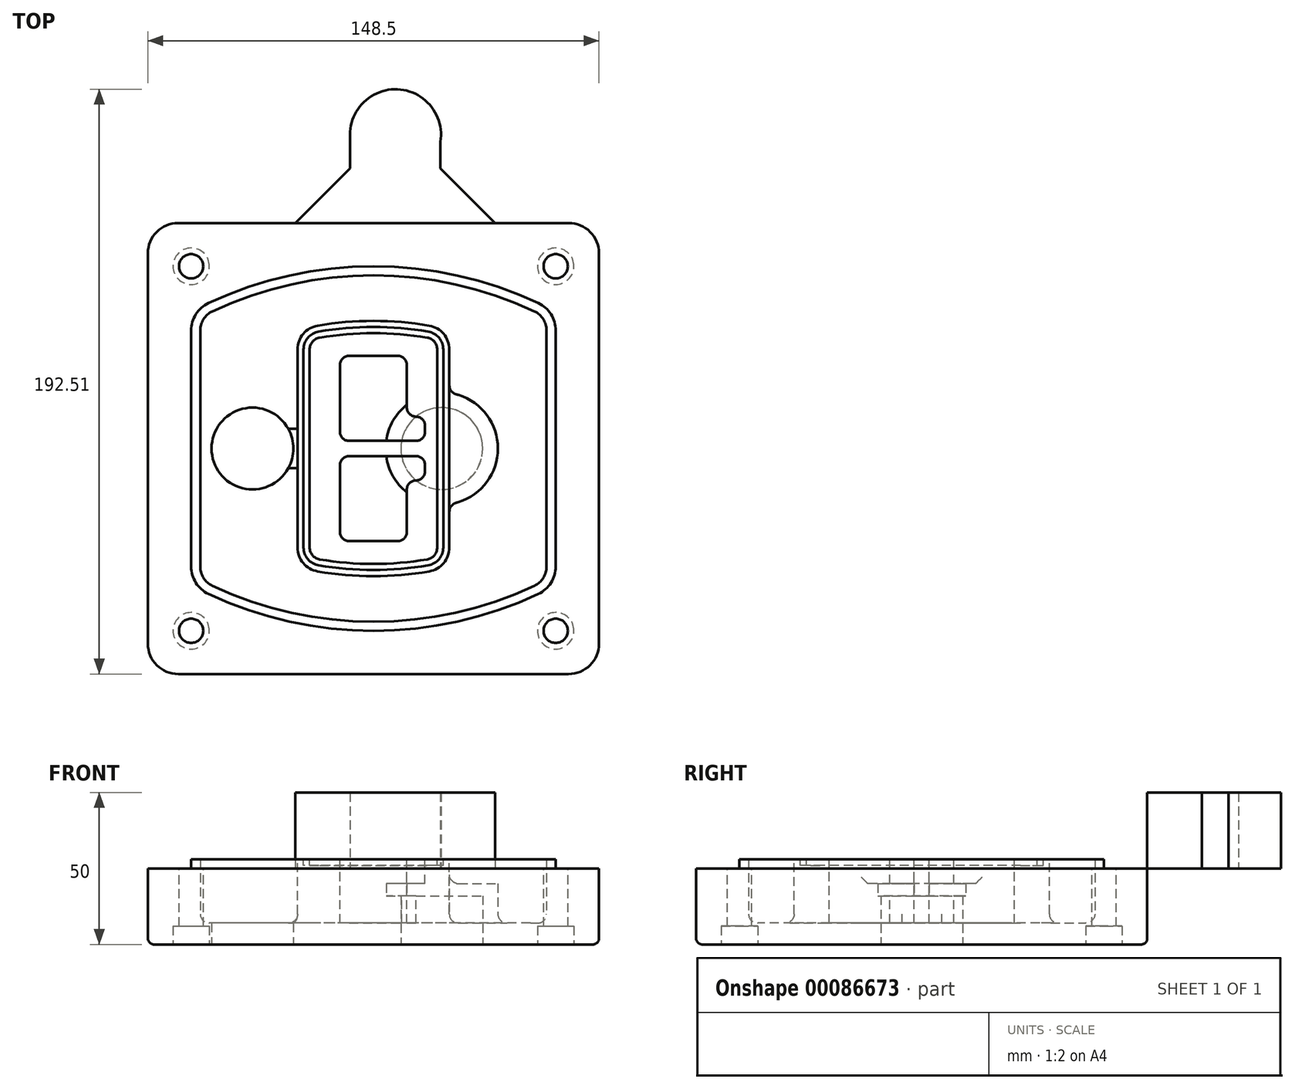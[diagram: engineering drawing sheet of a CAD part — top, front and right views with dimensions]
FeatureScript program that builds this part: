
annotation { "Feature Type Name" : "Feature", "Feature Type Description" : "" }
export const myFeature = defineFeature(function(context is Context, id is Id, definition is map)
    precondition{}
    {
        {
            var Q0;
            Q0=qCreatedBy(makeId("Top.planeOp"),FACE);
            var sketch = newSketch(context, id + "F0", { "sketchPlane" : qUnion([Q0])});
            skPoint(sketch, "E0.rect.middle", {"position": v(0, 0) * mm});
            skLineSegment(sketch, "E1.bottom", {"start": v(-64.25, -74.25) * mm, "end": v(64.25, -74.25) * mm});
            skLineSegment(sketch, "E1.top", {"start": v(-64.25, 74.25) * mm, "end": v(64.25, 74.25) * mm});
            skLineSegment(sketch, "E1.left", {"start": v(-74.25, -64.25) * mm, "end": v(-74.25, 64.25) * mm});
            skLineSegment(sketch, "E1.right", {"start": v(74.25, -64.25) * mm, "end": v(74.25, 64.25) * mm});
            skLineSegment(sketch, "E2", {"start": v(-74.25, 74.25) * mm, "end": v(74.25, -74.25) * mm, "construction": true});
            skLineSegment(sketch, "E3", {"start": v(74.25, 74.25) * mm, "end": v(-74.25, -74.25) * mm, "construction": true});
            skCircle(sketch, "E4", {"center": v(-60, 60) * mm, "radius": 4 * mm});
            skCircle(sketch, "E5", {"center": v(60, 60) * mm, "radius": 4 * mm});
            skCircle(sketch, "E6", {"center": v(60, -60) * mm, "radius": 4 * mm});
            skCircle(sketch, "E7", {"center": v(-60, -60) * mm, "radius": 4 * mm});
            skLineSegment(sketch, "E8", {"start": v(-60, 60) * mm, "end": v(60, 60) * mm, "construction": true});
            skLineSegment(sketch, "E9", {"start": v(60, 60) * mm, "end": v(60, -60) * mm, "construction": true});
            skLineSegment(sketch, "E10", {"start": v(60, -60) * mm, "end": v(-60, -60) * mm, "construction": true});
            skLineSegment(sketch, "E11", {"start": v(-60, -60) * mm, "end": v(-60, 60) * mm, "construction": true});
            skLineSegment(sketch, "E12", {"start": v(-60, 38.83) * mm, "end": v(-60, -38.83) * mm});
            skLineSegment(sketch, "E13", {"start": v(60, 38.83) * mm, "end": v(60, -38.83) * mm});
            skArc(sketch, "E14", {"start": v(54.26, 47.88) * mm, "mid": v(0, 60) * mm, "end": v(-54.26, 47.88) * mm});
            skArc(sketch, "E15", {"start": v(-54.26, -47.88) * mm, "mid": v(0, -60) * mm, "end": v(54.26, -47.88) * mm});
            skLineSegment(sketch, "E16", {"start": v(-60, 0) * mm, "end": v(60, 0) * mm, "construction": true});
            skPoint(sketch, "E17.visualSharp", {"position": v(-60, -45) * mm});
            skArc(sketch, "E17.filletArc", {"start": v(-60, -38.83) * mm, "mid": v(-58.44, -44.2) * mm, "end": v(-54.26, -47.88) * mm});
            skPoint(sketch, "E18.visualSharp", {"position": v(-60, 45) * mm});
            skArc(sketch, "E18.filletArc", {"start": v(-54.26, 47.88) * mm, "mid": v(-58.44, 44.2) * mm, "end": v(-60, 38.83) * mm});
            skPoint(sketch, "E19.visualSharp", {"position": v(60, 45) * mm});
            skArc(sketch, "E19.filletArc", {"start": v(60, 38.83) * mm, "mid": v(58.44, 44.2) * mm, "end": v(54.26, 47.88) * mm});
            skPoint(sketch, "E20.visualSharp", {"position": v(60, -45) * mm});
            skArc(sketch, "E20.filletArc", {"start": v(54.26, -47.88) * mm, "mid": v(58.44, -44.2) * mm, "end": v(60, -38.83) * mm});
            skPoint(sketch, "E21.visualSharp", {"position": v(-74.25, 74.25) * mm});
            skArc(sketch, "E21.filletArc", {"start": v(-64.25, 74.25) * mm, "mid": v(-71.32, 71.32) * mm, "end": v(-74.25, 64.25) * mm});
            skPoint(sketch, "E22.visualSharp", {"position": v(74.25, 74.25) * mm});
            skArc(sketch, "E22.filletArc", {"start": v(74.25, 64.25) * mm, "mid": v(71.32, 71.32) * mm, "end": v(64.25, 74.25) * mm});
            skPoint(sketch, "E23.visualSharp", {"position": v(74.25, -74.25) * mm});
            skArc(sketch, "E23.filletArc", {"start": v(64.25, -74.25) * mm, "mid": v(71.32, -71.32) * mm, "end": v(74.25, -64.25) * mm});
            skPoint(sketch, "E24.visualSharp", {"position": v(-74.25, -74.25) * mm});
            skArc(sketch, "E24.filletArc", {"start": v(-74.25, -64.25) * mm, "mid": v(-71.32, -71.32) * mm, "end": v(-64.25, -74.25) * mm});
            skArc(sketch, "E25.0", {"start": v(57, 38.83) * mm, "mid": v(55.9, 42.58) * mm, "end": v(52.98, 45.17) * mm});
            skLineSegment(sketch, "E25.1", {"start": v(57, 38.83) * mm, "end": v(57, -38.83) * mm});
            skArc(sketch, "E25.2", {"start": v(52.98, -45.17) * mm, "mid": v(55.9, -42.58) * mm, "end": v(57, -38.83) * mm});
            skArc(sketch, "E25.3", {"start": v(-52.98, -45.17) * mm, "mid": v(0, -57) * mm, "end": v(52.98, -45.17) * mm});
            skArc(sketch, "E25.4", {"start": v(-57, -38.83) * mm, "mid": v(-55.9, -42.58) * mm, "end": v(-52.98, -45.17) * mm});
            skArc(sketch, "E25.5", {"start": v(52.98, 45.17) * mm, "mid": v(0, 57) * mm, "end": v(-52.98, 45.17) * mm});
            skLineSegment(sketch, "E25.6", {"start": v(-57, 38.83) * mm, "end": v(-57, -38.83) * mm});
            skArc(sketch, "E25.7", {"start": v(-52.98, 45.17) * mm, "mid": v(-55.9, 42.58) * mm, "end": v(-57, 38.83) * mm});
            skArc(sketch, "E26.0", {"start": v(-55.96, 51.5) * mm, "mid": v(-61.82, 46.33) * mm, "end": v(-64, 38.83) * mm});
            skArc(sketch, "E26.1", {"start": v(55.96, 51.5) * mm, "mid": v(0, 64) * mm, "end": v(-55.96, 51.5) * mm});
            skArc(sketch, "E26.2", {"start": v(64, 38.83) * mm, "mid": v(61.82, 46.33) * mm, "end": v(55.96, 51.5) * mm});
            skLineSegment(sketch, "E26.3", {"start": v(64, 38.83) * mm, "end": v(64, -38.83) * mm});
            skArc(sketch, "E26.4", {"start": v(55.96, -51.5) * mm, "mid": v(61.82, -46.33) * mm, "end": v(64, -38.83) * mm});
            skLineSegment(sketch, "E26.5", {"start": v(-64, 38.83) * mm, "end": v(-64, -38.83) * mm});
            skArc(sketch, "E26.6", {"start": v(-55.96, -51.5) * mm, "mid": v(0, -64) * mm, "end": v(55.96, -51.5) * mm});
            skArc(sketch, "E26.7", {"start": v(-64, -38.83) * mm, "mid": v(-61.82, -46.33) * mm, "end": v(-55.96, -51.5) * mm});
            skSolve(sketch);
        }
        {
            var Q0;
            Q0=makeQuery(id+"F0.imprint","IMPRINT",FACE,{"disambiguationData":[TD([[makeQuery(id+"F0.imprint","IMPRINT",EDGE,{"derivedFrom":sQuery(id+"F0.wireOp",EDGE,"E1.bottom")}),1.0]])]});
            var Q1;
            Q1=makeQuery(id+"F0.imprint","IMPRINT",FACE,{"disambiguationData":[TD([[makeQuery(id+"F0.imprint","IMPRINT",EDGE,{"derivedFrom":sQuery(id+"F0.wireOp",EDGE,"E12")}),1.0]])]});
            var Q2;
            Q2=makeQuery(id+"F0.imprint","IMPRINT",FACE,{"disambiguationData":[TD([[makeQuery(id+"F0.imprint","IMPRINT",EDGE,{"derivedFrom":sQuery(id+"F0.wireOp",EDGE,"E25.0")}),1.0]])]});
            var Q3;
            Q3=makeQuery(id+"F0.imprint","IMPRINT",FACE,{"disambiguationData":[TD([[makeQuery(id+"F0.imprint","IMPRINT",EDGE,{"derivedFrom":sQuery(id+"F0.wireOp",EDGE,"E12")}),-1.0]])]});
            extrude(context, id + "F1", {"entities" : qUnion([Q0, Q1, Q2, Q3]), "oppositeDirection" : true, "depth" : 25 * mm});
        }
        {
            var Q0;
            Q0=makeQuery(id+"F0.imprint","IMPRINT",FACE,{"disambiguationData":[TD([[makeQuery(id+"F0.imprint","IMPRINT",EDGE,{"derivedFrom":sQuery(id+"F0.wireOp",EDGE,"E12")}),1.0]])]});
            extrude(context, id + "F2", {"entities" : qUnion([Q0]), "operationType" : NewBodyOperationType.ADD, "depth" : 3 * mm});
        }
        {
            var Q0;
            Q0=makeQuery(id+"F0.imprint","IMPRINT",FACE,{"disambiguationData":[TD([[makeQuery(id+"F0.imprint","IMPRINT",EDGE,{"derivedFrom":sQuery(id+"F0.wireOp",EDGE,"E25.0")}),1.0]])]});
            extrude(context, id + "F3", {"entities" : qUnion([Q0]), "operationType" : NewBodyOperationType.REMOVE, "oppositeDirection" : true, "depth" : 18 * mm});
        }
        {
            var Q0;
            Q0=makeQuery(id+"F2.opExtrude","CAP_FACE",FACE,{"disambiguationData":[OSD([sQuery(id+"F0.wireOp",EDGE,"E12"),sQuery(id+"F0.wireOp",EDGE,"E13"),sQuery(id+"F0.wireOp",EDGE,"E14"),sQuery(id+"F0.wireOp",EDGE,"E15"),sQuery(id+"F0.wireOp",EDGE,"E17.filletArc"),sQuery(id+"F0.wireOp",EDGE,"E18.filletArc"),sQuery(id+"F0.wireOp",EDGE,"E19.filletArc"),sQuery(id+"F0.wireOp",EDGE,"E20.filletArc"),sQuery(id+"F0.wireOp",EDGE,"E25.0"),sQuery(id+"F0.wireOp",EDGE,"E25.1"),sQuery(id+"F0.wireOp",EDGE,"E25.2"),sQuery(id+"F0.wireOp",EDGE,"E25.3"),sQuery(id+"F0.wireOp",EDGE,"E25.4"),sQuery(id+"F0.wireOp",EDGE,"E25.5"),sQuery(id+"F0.wireOp",EDGE,"E25.6"),sQuery(id+"F0.wireOp",EDGE,"E25.7")])],"isStart":false});
            var sketch = newSketch(context, id + "F4", { "sketchPlane" : qUnion([Q0])});
            skArc(sketch, "E27.0", {"start": v(-18.34, -40.45) * mm, "mid": v(0, -42) * mm, "end": v(18.34, -40.45) * mm});
            skArc(sketch, "E28.0", {"start": v(18.34, 40.45) * mm, "mid": v(0, 42) * mm, "end": v(-18.34, 40.45) * mm});
            skLineSegment(sketch, "E29", {"start": v(-25, 32.57) * mm, "end": v(-25, -32.57) * mm});
            skLineSegment(sketch, "E30", {"start": v(25, 32.57) * mm, "end": v(25, -32.57) * mm});
            skLineSegment(sketch, "E31", {"start": v(-25, 39.1) * mm, "end": v(25, 39.1) * mm, "construction": true});
            skLineSegment(sketch, "E32", {"start": v(-25, -39.1) * mm, "end": v(25, -39.1) * mm, "construction": true});
            skPoint(sketch, "E33.visualSharp", {"position": v(-25, 39.1) * mm});
            skArc(sketch, "E33.filletArc", {"start": v(-18.34, 40.45) * mm, "mid": v(-23.11, 37.73) * mm, "end": v(-25, 32.57) * mm});
            skPoint(sketch, "E34.visualSharp", {"position": v(25, 39.1) * mm});
            skArc(sketch, "E34.filletArc", {"start": v(25, 32.57) * mm, "mid": v(23.11, 37.73) * mm, "end": v(18.34, 40.45) * mm});
            skPoint(sketch, "E35.visualSharp", {"position": v(25, -39.1) * mm});
            skArc(sketch, "E35.filletArc", {"start": v(18.34, -40.45) * mm, "mid": v(23.11, -37.73) * mm, "end": v(25, -32.57) * mm});
            skPoint(sketch, "E36.visualSharp", {"position": v(-25, -39.1) * mm});
            skArc(sketch, "E36.filletArc", {"start": v(-25, -32.57) * mm, "mid": v(-23.11, -37.73) * mm, "end": v(-18.34, -40.45) * mm});
            skArc(sketch, "E37.0", {"start": v(52.98, 45.17) * mm, "mid": v(0, 57) * mm, "end": v(-52.98, 45.17) * mm});
            skArc(sketch, "E37.1", {"start": v(-52.98, 45.17) * mm, "mid": v(-55.9, 42.58) * mm, "end": v(-57, 38.83) * mm});
            skLineSegment(sketch, "E37.2", {"start": v(-57, 38.83) * mm, "end": v(-57, -38.83) * mm});
            skArc(sketch, "E37.3", {"start": v(-57, -38.83) * mm, "mid": v(-55.9, -42.58) * mm, "end": v(-52.98, -45.17) * mm});
            skArc(sketch, "E37.4", {"start": v(-52.98, -45.17) * mm, "mid": v(0, -57) * mm, "end": v(52.98, -45.17) * mm});
            skArc(sketch, "E37.5", {"start": v(52.98, -45.17) * mm, "mid": v(55.9, -42.58) * mm, "end": v(57, -38.83) * mm});
            skLineSegment(sketch, "E37.6", {"start": v(57, 38.83) * mm, "end": v(57, -38.83) * mm});
            skArc(sketch, "E37.7", {"start": v(57, 38.83) * mm, "mid": v(55.9, 42.58) * mm, "end": v(52.98, 45.17) * mm});
            skLineSegment(sketch, "E38.0", {"start": v(23, 32.57) * mm, "end": v(23, -32.57) * mm});
            skArc(sketch, "E38.1", {"start": v(18, -38.48) * mm, "mid": v(21.58, -36.44) * mm, "end": v(23, -32.57) * mm});
            skArc(sketch, "E38.2", {"start": v(-18, -38.48) * mm, "mid": v(0, -40) * mm, "end": v(18, -38.48) * mm});
            skArc(sketch, "E38.3", {"start": v(-23, -32.57) * mm, "mid": v(-21.58, -36.44) * mm, "end": v(-18, -38.48) * mm});
            skLineSegment(sketch, "E38.4", {"start": v(-23, 32.57) * mm, "end": v(-23, -32.57) * mm});
            skArc(sketch, "E38.5", {"start": v(23, 32.57) * mm, "mid": v(21.58, 36.44) * mm, "end": v(18, 38.48) * mm});
            skArc(sketch, "E38.6", {"start": v(-18, 38.48) * mm, "mid": v(-21.58, 36.44) * mm, "end": v(-23, 32.57) * mm});
            skArc(sketch, "E38.7", {"start": v(18, 38.48) * mm, "mid": v(0, 40) * mm, "end": v(-18, 38.48) * mm});
            skArc(sketch, "E39.0", {"start": v(21, 32.57) * mm, "mid": v(20.06, 35.15) * mm, "end": v(17.67, 36.5) * mm});
            skLineSegment(sketch, "E39.1", {"start": v(21, 32.57) * mm, "end": v(21, -32.57) * mm});
            skArc(sketch, "E39.2", {"start": v(17.67, -36.5) * mm, "mid": v(20.06, -35.15) * mm, "end": v(21, -32.57) * mm});
            skArc(sketch, "E39.3", {"start": v(-17.67, -36.5) * mm, "mid": v(0, -38) * mm, "end": v(17.67, -36.5) * mm});
            skArc(sketch, "E39.4", {"start": v(-21, -32.57) * mm, "mid": v(-20.06, -35.15) * mm, "end": v(-17.67, -36.5) * mm});
            skArc(sketch, "E39.5", {"start": v(17.67, 36.5) * mm, "mid": v(0, 38) * mm, "end": v(-17.67, 36.5) * mm});
            skLineSegment(sketch, "E39.6", {"start": v(-21, 32.57) * mm, "end": v(-21, -32.57) * mm});
            skArc(sketch, "E39.7", {"start": v(-17.67, 36.5) * mm, "mid": v(-20.06, 35.15) * mm, "end": v(-21, 32.57) * mm});
            skLineSegment(sketch, "E40", {"start": v(-25, 0) * mm, "end": v(25, 0) * mm, "construction": true});
            skLineSegment(sketch, "E41", {"start": v(-11, 5.5) * mm, "end": v(-11, 27.5) * mm});
            skLineSegment(sketch, "E42", {"start": v(-8, 30.5) * mm, "end": v(8, 30.5) * mm});
            skLineSegment(sketch, "E43", {"start": v(11, 27.5) * mm, "end": v(11, 13.5) * mm});
            skLineSegment(sketch, "E44", {"start": v(14, 10.5) * mm, "end": v(14, 10.5) * mm});
            skLineSegment(sketch, "E45", {"start": v(17, 7.5) * mm, "end": v(17, 5.5) * mm});
            skLineSegment(sketch, "E46", {"start": v(14, 2.5) * mm, "end": v(-8, 2.5) * mm});
            skPoint(sketch, "E47.visualSharp", {"position": v(-11, 30.5) * mm});
            skArc(sketch, "E47.filletArc", {"start": v(-8, 30.5) * mm, "mid": v(-10.12, 29.62) * mm, "end": v(-11, 27.5) * mm});
            skPoint(sketch, "E48.visualSharp", {"position": v(11, 30.5) * mm});
            skArc(sketch, "E48.filletArc", {"start": v(11, 27.5) * mm, "mid": v(10.12, 29.62) * mm, "end": v(8, 30.5) * mm});
            skPoint(sketch, "E49.visualSharp", {"position": v(11, 10.5) * mm});
            skArc(sketch, "E49.filletArc", {"start": v(11, 13.5) * mm, "mid": v(11.88, 11.38) * mm, "end": v(14, 10.5) * mm});
            skPoint(sketch, "E50.visualSharp", {"position": v(17, 10.5) * mm});
            skArc(sketch, "E50.filletArc", {"start": v(17, 7.5) * mm, "mid": v(16.12, 9.62) * mm, "end": v(14, 10.5) * mm});
            skPoint(sketch, "E51.visualSharp", {"position": v(17, 2.5) * mm});
            skArc(sketch, "E51.filletArc", {"start": v(14, 2.5) * mm, "mid": v(16.12, 3.38) * mm, "end": v(17, 5.5) * mm});
            skPoint(sketch, "E52.visualSharp", {"position": v(-11, 2.5) * mm});
            skArc(sketch, "E52.filletArc", {"start": v(-11, 5.5) * mm, "mid": v(-10.12, 3.38) * mm, "end": v(-8, 2.5) * mm});
            skLineSegment(sketch, "E53.0.MirrorCS", {"start": v(14, -2.5) * mm, "end": v(-8, -2.5) * mm});
            skArc(sketch, "E54.0.MirrorCS", {"start": v(-11, -5.5) * mm, "mid": v(-10.12, -3.38) * mm, "end": v(-8, -2.5) * mm});
            skLineSegment(sketch, "E55.0.MirrorCS", {"start": v(-11, -5.5) * mm, "end": v(-11, -27.5) * mm});
            skArc(sketch, "E56.0.MirrorCS", {"start": v(-8, -30.5) * mm, "mid": v(-10.12, -29.62) * mm, "end": v(-11, -27.5) * mm});
            skLineSegment(sketch, "E57.0.MirrorCS", {"start": v(-8, -30.5) * mm, "end": v(8, -30.5) * mm});
            skArc(sketch, "E58.0.MirrorCS", {"start": v(11, -27.5) * mm, "mid": v(10.12, -29.62) * mm, "end": v(8, -30.5) * mm});
            skLineSegment(sketch, "E59.0.MirrorCS", {"start": v(11, -27.5) * mm, "end": v(11, -13.5) * mm});
            skArc(sketch, "E60.0.MirrorCS", {"start": v(11, -13.5) * mm, "mid": v(11.88, -11.38) * mm, "end": v(14, -10.5) * mm});
            skArc(sketch, "E61.0.MirrorCS", {"start": v(17, -7.5) * mm, "mid": v(16.12, -9.62) * mm, "end": v(14, -10.5) * mm});
            skLineSegment(sketch, "E62.0.MirrorCS", {"start": v(17, -7.5) * mm, "end": v(17, -5.5) * mm});
            skArc(sketch, "E63.0.MirrorCS", {"start": v(14, -2.5) * mm, "mid": v(16.12, -3.38) * mm, "end": v(17, -5.5) * mm});
            skSolve(sketch);
        }
        {
            var Q0;
            Q0=makeQuery(id+"F4.imprint","IMPRINT",FACE,{"disambiguationData":[TD([[makeQuery(id+"F4.imprint","IMPRINT",EDGE,{"derivedFrom":sQuery(id+"F4.wireOp",EDGE,"E27.0")}),1.0]])]});
            var Q1;
            Q1=makeQuery(id+"F4.imprint","IMPRINT",FACE,{"disambiguationData":[TD([[makeQuery(id+"F4.imprint","IMPRINT",EDGE,{"derivedFrom":sQuery(id+"F4.wireOp",EDGE,"E38.0")}),-1.0]])]});
            var Q2;
            Q2=makeQuery(id+"F4.imprint","IMPRINT",FACE,{"disambiguationData":[TD([[makeQuery(id+"F4.imprint","IMPRINT",EDGE,{"derivedFrom":sQuery(id+"F4.wireOp",EDGE,"E39.0")}),1.0]])]});
            extrude(context, id + "F5", {"entities" : qUnion([Q0, Q1, Q2]), "operationType" : NewBodyOperationType.ADD, "endBound" : BoundingType.UP_TO_NEXT, "oppositeDirection" : true, "depth" : 25 * mm});
        }
        {
            var Q0;
            Q0=makeQuery(id+"F4.imprint","IMPRINT",FACE,{"disambiguationData":[TD([[makeQuery(id+"F4.imprint","IMPRINT",EDGE,{"derivedFrom":sQuery(id+"F4.wireOp",EDGE,"E38.0")}),-1.0]])]});
            extrude(context, id + "F6", {"entities" : qUnion([Q0]), "operationType" : NewBodyOperationType.REMOVE, "oppositeDirection" : true, "depth" : 2 * mm});
        }
        {
            var Q0;
            Q0=makeQuery(id+"F1.opExtrude","CAP_FACE",FACE,{"disambiguationData":[OSD([sQuery(id+"F0.wireOp",EDGE,"E1.bottom"),sQuery(id+"F0.wireOp",EDGE,"E1.top"),sQuery(id+"F0.wireOp",EDGE,"E1.left"),sQuery(id+"F0.wireOp",EDGE,"E1.right"),sQuery(id+"F0.wireOp",EDGE,"E4"),sQuery(id+"F0.wireOp",EDGE,"E5"),sQuery(id+"F0.wireOp",EDGE,"E6"),sQuery(id+"F0.wireOp",EDGE,"E7"),sQuery(id+"F0.wireOp",EDGE,"E21.filletArc"),sQuery(id+"F0.wireOp",EDGE,"E22.filletArc"),sQuery(id+"F0.wireOp",EDGE,"E23.filletArc"),sQuery(id+"F0.wireOp",EDGE,"E24.filletArc")])],"isStart":false});
            var sketch = newSketch(context, id + "F7", { "sketchPlane" : qUnion([Q0])});
            skCircle(sketch, "E64", {"center": v(22.5, 0) * mm, "radius": 13.47 * mm});
            skCircle(sketch, "E65", {"center": v(-39.81, 0) * mm, "radius": 13.47 * mm});
            skLineSegment(sketch, "E66", {"start": v(74.25, 0) * mm, "end": v(-74.25, 0) * mm});
            skCircle(sketch, "E67", {"center": v(22.5, 0) * mm, "radius": 18.47 * mm});
            skCircle(sketch, "E68", {"center": v(60, -60) * mm, "radius": 6 * mm});
            skCircle(sketch, "E69", {"center": v(-60, -60) * mm, "radius": 6 * mm});
            skCircle(sketch, "E70", {"center": v(-60, 60) * mm, "radius": 6 * mm});
            skCircle(sketch, "E71", {"center": v(60, 60) * mm, "radius": 6 * mm});
            skSolve(sketch);
        }
        {
            var Q0;
            {var subQ1=sQuery(id+"F7.wireOp",EDGE,"E66");var subQ4=sQuery(id+"F7.wireOp",EDGE,"E64");var subQ6=makeQuery(id+"F7.imprint","INTERSECT",VERTEX,{"disambiguationData":[OD(0.0)],"derivedFrom":[subQ4,subQ1]});Q0=makeQuery(id+"F7.imprint","IMPRINT",FACE,{"disambiguationData":[TD([[makeQuery(id+"F7.imprint","IMPRINT",EDGE,{"disambiguationData":[TD([[subQ6,-1.0]])],"derivedFrom":subQ4}),-1.0]])]});}
            var Q1;
            {var subQ0=sQuery(id+"F7.wireOp",EDGE,"E66");var subQ1=sQuery(id+"F7.wireOp",EDGE,"E64");var subQ3=makeQuery(id+"F7.imprint","INTERSECT",VERTEX,{"disambiguationData":[OD(0.0)],"derivedFrom":[subQ1,subQ0]});Q1=makeQuery(id+"F7.imprint","IMPRINT",FACE,{"disambiguationData":[TD([[makeQuery(id+"F7.imprint","IMPRINT",EDGE,{"disambiguationData":[TD([[subQ3,-1.0]])],"derivedFrom":subQ1}),1.0]])]});}
            var Q2;
            {var subQ0=sQuery(id+"F7.wireOp",EDGE,"E66");var subQ1=sQuery(id+"F7.wireOp",EDGE,"E64");var subQ3=makeQuery(id+"F7.imprint","INTERSECT",VERTEX,{"disambiguationData":[OD(0.0)],"derivedFrom":[subQ1,subQ0]});Q2=makeQuery(id+"F7.imprint","IMPRINT",FACE,{"disambiguationData":[TD([[makeQuery(id+"F7.imprint","IMPRINT",EDGE,{"disambiguationData":[TD([[subQ3,1.0]])],"derivedFrom":subQ1}),1.0]])]});}
            var Q3;
            {var subQ1=sQuery(id+"F7.wireOp",EDGE,"E66");var subQ4=sQuery(id+"F7.wireOp",EDGE,"E64");var subQ6=makeQuery(id+"F7.imprint","INTERSECT",VERTEX,{"disambiguationData":[OD(0.0)],"derivedFrom":[subQ4,subQ1]});Q3=makeQuery(id+"F7.imprint","IMPRINT",FACE,{"disambiguationData":[TD([[makeQuery(id+"F7.imprint","IMPRINT",EDGE,{"disambiguationData":[TD([[subQ6,1.0]])],"derivedFrom":subQ4}),-1.0]])]});}
            extrude(context, id + "F8", {"entities" : qUnion([Q0, Q1, Q2, Q3]), "operationType" : NewBodyOperationType.ADD, "oppositeDirection" : true, "depth" : 20 * mm});
        }
        {
            var Q0;
            {var subQ0=sQuery(id+"F7.wireOp",EDGE,"E66");var subQ1=sQuery(id+"F7.wireOp",EDGE,"E64");var subQ3=makeQuery(id+"F7.imprint","INTERSECT",VERTEX,{"disambiguationData":[OD(0.0)],"derivedFrom":[subQ1,subQ0]});Q0=makeQuery(id+"F7.imprint","IMPRINT",FACE,{"disambiguationData":[TD([[makeQuery(id+"F7.imprint","IMPRINT",EDGE,{"disambiguationData":[TD([[subQ3,-1.0]])],"derivedFrom":subQ1}),1.0]])]});}
            var Q1;
            {var subQ0=sQuery(id+"F7.wireOp",EDGE,"E66");var subQ1=sQuery(id+"F7.wireOp",EDGE,"E64");var subQ3=makeQuery(id+"F7.imprint","INTERSECT",VERTEX,{"disambiguationData":[OD(0.0)],"derivedFrom":[subQ1,subQ0]});Q1=makeQuery(id+"F7.imprint","IMPRINT",FACE,{"disambiguationData":[TD([[makeQuery(id+"F7.imprint","IMPRINT",EDGE,{"disambiguationData":[TD([[subQ3,1.0]])],"derivedFrom":subQ1}),1.0]])]});}
            extrude(context, id + "F9", {"entities" : qUnion([Q0, Q1]), "operationType" : NewBodyOperationType.REMOVE, "oppositeDirection" : true, "depth" : 16 * mm});
        }
        {
            var Q0;
            {var subQ0=sQuery(id+"F7.wireOp",EDGE,"E66");var subQ1=sQuery(id+"F7.wireOp",EDGE,"E65");var subQ3=makeQuery(id+"F7.imprint","INTERSECT",VERTEX,{"disambiguationData":[OD(0.0)],"derivedFrom":[subQ1,subQ0]});Q0=makeQuery(id+"F7.imprint","IMPRINT",FACE,{"disambiguationData":[TD([[makeQuery(id+"F7.imprint","IMPRINT",EDGE,{"disambiguationData":[TD([[subQ3,-1.0]])],"derivedFrom":subQ1}),1.0]])]});}
            var Q1;
            {var subQ0=sQuery(id+"F7.wireOp",EDGE,"E66");var subQ1=sQuery(id+"F7.wireOp",EDGE,"E65");var subQ3=makeQuery(id+"F7.imprint","INTERSECT",VERTEX,{"disambiguationData":[OD(0.0)],"derivedFrom":[subQ1,subQ0]});Q1=makeQuery(id+"F7.imprint","IMPRINT",FACE,{"disambiguationData":[TD([[makeQuery(id+"F7.imprint","IMPRINT",EDGE,{"disambiguationData":[TD([[subQ3,1.0]])],"derivedFrom":subQ1}),1.0]])]});}
            extrude(context, id + "F10", {"entities" : qUnion([Q0, Q1]), "operationType" : NewBodyOperationType.REMOVE, "oppositeDirection" : true, "depth" : 25 * mm});
        }
        {
            var Q0;
            Q0=makeQuery(id+"F7.imprint","IMPRINT",FACE,{"disambiguationData":[TD([[makeQuery(id+"F7.imprint","IMPRINT",EDGE,{"derivedFrom":sQuery(id+"F7.wireOp",EDGE,"E68")}),1.0]])]});
            var Q1;
            Q1=makeQuery(id+"F7.imprint","IMPRINT",FACE,{"disambiguationData":[TD([[makeQuery(id+"F7.imprint","IMPRINT",EDGE,{"derivedFrom":makeQuery(id+"F1.opExtrude","CAP_EDGE",EDGE,{"disambiguationData":[OSD([sQuery(id+"F0.wireOp",EDGE,"E5")])],"isStart":false})}),-1.0]])]});
            var Q2;
            Q2=makeQuery(id+"F7.imprint","IMPRINT",FACE,{"disambiguationData":[TD([[makeQuery(id+"F7.imprint","IMPRINT",EDGE,{"derivedFrom":sQuery(id+"F7.wireOp",EDGE,"E69")}),1.0]])]});
            var Q3;
            Q3=makeQuery(id+"F7.imprint","IMPRINT",FACE,{"disambiguationData":[TD([[makeQuery(id+"F7.imprint","IMPRINT",EDGE,{"derivedFrom":makeQuery(id+"F1.opExtrude","CAP_EDGE",EDGE,{"disambiguationData":[OSD([sQuery(id+"F0.wireOp",EDGE,"E4")])],"isStart":false})}),-1.0]])]});
            var Q4;
            Q4=makeQuery(id+"F7.imprint","IMPRINT",FACE,{"disambiguationData":[TD([[makeQuery(id+"F7.imprint","IMPRINT",EDGE,{"derivedFrom":sQuery(id+"F7.wireOp",EDGE,"E70")}),1.0]])]});
            var Q5;
            Q5=makeQuery(id+"F7.imprint","IMPRINT",FACE,{"disambiguationData":[TD([[makeQuery(id+"F7.imprint","IMPRINT",EDGE,{"derivedFrom":makeQuery(id+"F1.opExtrude","CAP_EDGE",EDGE,{"disambiguationData":[OSD([sQuery(id+"F0.wireOp",EDGE,"E7")])],"isStart":false})}),-1.0]])]});
            var Q6;
            Q6=makeQuery(id+"F7.imprint","IMPRINT",FACE,{"disambiguationData":[TD([[makeQuery(id+"F7.imprint","IMPRINT",EDGE,{"derivedFrom":sQuery(id+"F7.wireOp",EDGE,"E71")}),1.0]])]});
            var Q7;
            Q7=makeQuery(id+"F7.imprint","IMPRINT",FACE,{"disambiguationData":[TD([[makeQuery(id+"F7.imprint","IMPRINT",EDGE,{"derivedFrom":makeQuery(id+"F1.opExtrude","CAP_EDGE",EDGE,{"disambiguationData":[OSD([sQuery(id+"F0.wireOp",EDGE,"E6")])],"isStart":false})}),-1.0]])]});
            extrude(context, id + "F11", {"entities" : qUnion([Q0, Q1, Q2, Q3, Q4, Q5, Q6, Q7]), "operationType" : NewBodyOperationType.REMOVE, "oppositeDirection" : true, "depth" : 6 * mm});
        }
        {
            var Q0;
            Q0=makeQuery(id+"F9.boolean.opBoolean","COPY",FACE,{"derivedFrom":makeQuery(id+"F9.opExtrude","CAP_FACE",FACE,{"disambiguationData":[OSD([sQuery(id+"F7.wireOp",EDGE,"E64")])],"isStart":false})});
            var sketch = newSketch(context, id + "F12", { "sketchPlane" : qUnion([Q0])});
            skArc(sketch, "E72.0", {"start": v(11, 14.45) * mm, "mid": v(6.45, 9.13) * mm, "end": v(4.2, 2.5) * mm});
            skArc(sketch, "E72.1", {"start": v(4.2, -2.5) * mm, "mid": v(6.45, -9.13) * mm, "end": v(11, -14.45) * mm});
            skLineSegment(sketch, "E73", {"start": v(4.2, -2.5) * mm, "end": v(14, -2.5) * mm});
            skLineSegment(sketch, "E74.0", {"start": v(14, 2.5) * mm, "end": v(4.2, 2.5) * mm});
            skArc(sketch, "E74.1", {"start": v(14, 2.5) * mm, "mid": v(16.12, 3.38) * mm, "end": v(17, 5.5) * mm});
            skLineSegment(sketch, "E74.2", {"start": v(17, 7.5) * mm, "end": v(17, 5.5) * mm});
            skArc(sketch, "E74.3", {"start": v(17, 7.5) * mm, "mid": v(16.12, 9.62) * mm, "end": v(14, 10.5) * mm});
            skArc(sketch, "E74.4", {"start": v(11, 13.5) * mm, "mid": v(11.88, 11.38) * mm, "end": v(14, 10.5) * mm});
            skLineSegment(sketch, "E74.5", {"start": v(11, 14.45) * mm, "end": v(11, 13.5) * mm});
            skLineSegment(sketch, "E74.7", {"start": v(14, -2.5) * mm, "end": v(4.2, -2.5) * mm});
            skArc(sketch, "E74.8", {"start": v(14, -2.5) * mm, "mid": v(16.12, -3.38) * mm, "end": v(17, -5.5) * mm});
            skLineSegment(sketch, "E74.9", {"start": v(17, -7.5) * mm, "end": v(17, -5.5) * mm});
            skArc(sketch, "E74.10", {"start": v(17, -7.5) * mm, "mid": v(16.12, -9.62) * mm, "end": v(14, -10.5) * mm});
            skArc(sketch, "E74.11", {"start": v(11, -13.5) * mm, "mid": v(11.88, -11.38) * mm, "end": v(14, -10.5) * mm});
            skLineSegment(sketch, "E74.12", {"start": v(11, -14.45) * mm, "end": v(11, -13.5) * mm});
            skPoint(sketch, "E75.orphan", {"position": v(11, -27.5) * mm});
            skPoint(sketch, "E76.orphan", {"position": v(-8, -2.5) * mm});
            skPoint(sketch, "E77.orphan", {"position": v(-8, 2.5) * mm});
            skPoint(sketch, "E78.orphan", {"position": v(11, 27.5) * mm});
            skSolve(sketch);
        }
        {
            var Q0;
            {var subQ7=sQuery(id+"F12.wireOp",EDGE,"E72.0");var subQ14=sQuery(id+"F12.wireOp",EDGE,"E72.1");var subQ16=sQuery(id+"F12.wireOp",EDGE,"E74.1");var subQ18=sQuery(id+"F12.wireOp",EDGE,"E74.8");Q0=qUnion([makeQuery(id+"F12.imprint","IMPRINT",FACE,{"disambiguationData":[TD([[makeQuery(id+"F12.imprint","IMPRINT",EDGE,{"derivedFrom":subQ7}),1.0]])]}),makeQuery(id+"F12.imprint","IMPRINT",FACE,{"disambiguationData":[TD([[makeQuery(id+"F12.imprint","IMPRINT",EDGE,{"derivedFrom":subQ14}),1.0]])]}),makeQuery(id+"F12.imprint","IMPRINT",FACE,{"disambiguationData":[TD([[makeQuery(id+"F12.imprint","IMPRINT",EDGE,{"derivedFrom":subQ16}),1.0]])]}),makeQuery(id+"F12.imprint","IMPRINT",FACE,{"disambiguationData":[TD([[makeQuery(id+"F12.imprint","IMPRINT",EDGE,{"derivedFrom":subQ18}),-1.0]])]})]);}
            var Q1;
            Q1=makeQuery(id+"F5.boolean.opBoolean","SPLIT",FACE,{"disambiguationData":[TD([makeQuery(id+"F5.opExtrude","SWEPT_FACE",FACE,{"disambiguationData":[OSD([sQuery(id+"F4.wireOp",EDGE,"E41")])]})])],"derivedFrom":makeQuery(id+"F3.boolean.opBoolean","COPY",FACE,{"derivedFrom":makeQuery(id+"F3.opExtrude","CAP_FACE",FACE,{"disambiguationData":[OSD([sQuery(id+"F0.wireOp",EDGE,"E25.0"),sQuery(id+"F0.wireOp",EDGE,"E25.1"),sQuery(id+"F0.wireOp",EDGE,"E25.2"),sQuery(id+"F0.wireOp",EDGE,"E25.3"),sQuery(id+"F0.wireOp",EDGE,"E25.4"),sQuery(id+"F0.wireOp",EDGE,"E25.5"),sQuery(id+"F0.wireOp",EDGE,"E25.6"),sQuery(id+"F0.wireOp",EDGE,"E25.7")])],"isStart":false})})});
            extrude(context, id + "F13", {"entities" : qUnion([Q0]), "operationType" : NewBodyOperationType.REMOVE, "endBound" : BoundingType.UP_TO_SURFACE, "endBoundEntityFace" : qUnion([Q1]), "depth" : 25 * mm});
        }
        {
            var Q0;
            Q0=makeQuery(id+"F3.boolean.opBoolean","COPY",EDGE,{"derivedFrom":makeQuery(id+"F3.opExtrude","CAP_EDGE",EDGE,{"disambiguationData":[OSD([sQuery(id+"F0.wireOp",EDGE,"E25.6")])],"isStart":false})});
            var Q1;
            Q1=makeQuery(id+"F8.boolean.opBoolean","INTERSECT",EDGE,{"derivedFrom":[makeQuery(id+"F5.opExtrude","SWEPT_FACE",FACE,{"disambiguationData":[OSD([sQuery(id+"F4.wireOp",EDGE,"E30")])]}),makeQuery(id+"F8.opExtrude","CAP_FACE",FACE,{"disambiguationData":[OSD([sQuery(id+"F7.wireOp",EDGE,"E67")])],"isStart":false})]});
            var Q2;
            Q2=makeQuery(id+"F8.boolean.opBoolean","INTERSECT",EDGE,{"disambiguationData":[OD(1.0)],"derivedFrom":[makeQuery(id+"F5.opExtrude","SWEPT_FACE",FACE,{"disambiguationData":[OSD([sQuery(id+"F4.wireOp",EDGE,"E30")])]}),makeQuery(id+"F8.opExtrude","SWEPT_FACE",FACE,{"disambiguationData":[OSD([sQuery(id+"F7.wireOp",EDGE,"E67")])]})]});
            var Q3;
            {var subQ0=sQuery(id+"F4.wireOp",EDGE,"E30");Q3=makeQuery(id+"F8.boolean.opBoolean","SPLIT",EDGE,{"disambiguationData":[TD([makeQuery(id+"F5.opExtrude","SWEPT_FACE",FACE,{"disambiguationData":[OSD([sQuery(id+"F4.wireOp",EDGE,"E35.filletArc")])]})])],"derivedFrom":makeQuery(id+"F5.opExtrude","CAP_EDGE",EDGE,{"disambiguationData":[OSD([subQ0])],"isStart":false})});}
            var Q4;
            {var subQ0=sQuery(id+"F0.wireOp",EDGE,"E25.7");var subQ1=sQuery(id+"F0.wireOp",EDGE,"E25.1");var subQ2=sQuery(id+"F0.wireOp",EDGE,"E25.6");var subQ3=sQuery(id+"F0.wireOp",EDGE,"E25.5");var subQ4=sQuery(id+"F0.wireOp",EDGE,"E25.4");var subQ5=sQuery(id+"F0.wireOp",EDGE,"E25.0");var subQ6=sQuery(id+"F0.wireOp",EDGE,"E25.2");var subQ7=sQuery(id+"F0.wireOp",EDGE,"E25.3");Q4=makeQuery(id+"F8.boolean.opBoolean","INTERSECT",EDGE,{"derivedFrom":[makeQuery(id+"F5.boolean.opBoolean","SPLIT",FACE,{"disambiguationData":[TD([makeQuery(id+"F2.opExtrude","SWEPT_FACE",FACE,{"disambiguationData":[OSD([subQ5])]})])],"derivedFrom":makeQuery(id+"F3.boolean.opBoolean","COPY",FACE,{"derivedFrom":makeQuery(id+"F3.opExtrude","CAP_FACE",FACE,{"disambiguationData":[OSD([subQ5,subQ1,subQ6,subQ7,subQ4,subQ3,subQ2,subQ0])],"isStart":false})})}),makeQuery(id+"F8.opExtrude","SWEPT_FACE",FACE,{"disambiguationData":[OSD([sQuery(id+"F7.wireOp",EDGE,"E67")])]})]});}
            var Q5;
            Q5=makeQuery(id+"F8.boolean.opBoolean","INTERSECT",EDGE,{"disambiguationData":[OD(0.0)],"derivedFrom":[makeQuery(id+"F5.opExtrude","SWEPT_FACE",FACE,{"disambiguationData":[OSD([sQuery(id+"F4.wireOp",EDGE,"E30")])]}),makeQuery(id+"F8.opExtrude","SWEPT_FACE",FACE,{"disambiguationData":[OSD([sQuery(id+"F7.wireOp",EDGE,"E67")])]})]});
            fillet(context, id + "F14", {"entities" : qUnion([Q0, Q1, Q2, Q3, Q4, Q5]), "radius" : 3 * mm, "tangentPropagation" : true, "allowEdgeOverflow" : false});
        }
        {
            var Q0;
            Q0=makeQuery(id+"F1.opExtrude","CAP_EDGE",EDGE,{"disambiguationData":[OSD([sQuery(id+"F0.wireOp",EDGE,"E1.bottom")])],"isStart":false});
            fillet(context, id + "F15", {"entities" : qUnion([Q0]), "radius" : 2 * mm, "tangentPropagation" : true, "allowEdgeOverflow" : false});
        }
        {
            var Q0;
            {var subQ0=sQuery(id+"F0.wireOp",EDGE,"E22.filletArc");var subQ1=sQuery(id+"F0.wireOp",EDGE,"E7");var subQ2=sQuery(id+"F0.wireOp",EDGE,"E6");var subQ3=sQuery(id+"F0.wireOp",EDGE,"E5");var subQ4=sQuery(id+"F0.wireOp",EDGE,"E4");var subQ5=sQuery(id+"F0.wireOp",EDGE,"E1.bottom");var subQ6=sQuery(id+"F0.wireOp",EDGE,"E21.filletArc");var subQ7=sQuery(id+"F0.wireOp",EDGE,"E1.top");var subQ8=sQuery(id+"F0.wireOp",EDGE,"E1.left");var subQ9=sQuery(id+"F0.wireOp",EDGE,"E1.right");var subQ10=sQuery(id+"F0.wireOp",EDGE,"E23.filletArc");var subQ11=sQuery(id+"F0.wireOp",EDGE,"E24.filletArc");Q0=makeQuery(id+"F2.boolean.opBoolean","SPLIT",FACE,{"disambiguationData":[TD([makeQuery(id+"F1.opExtrude","SWEPT_FACE",FACE,{"disambiguationData":[OSD([subQ5])]})])],"derivedFrom":makeQuery(id+"F1.opExtrude","CAP_FACE",FACE,{"disambiguationData":[OSD([subQ5,subQ7,subQ8,subQ9,subQ4,subQ3,subQ2,subQ1,subQ6,subQ0,subQ10,subQ11])],"isStart":true})});}
            var sketch = newSketch(context, id + "F16", { "sketchPlane" : qUnion([Q0])});
            skLineSegment(sketch, "E79", {"start": v(0, 74.25) * mm, "end": v(0, 104.25) * mm});
            skLineSegment(sketch, "E80", {"start": v(-25.7, 74.25) * mm, "end": v(-7.7, 92.25) * mm});
            skLineSegment(sketch, "E81", {"start": v(40.1, 74.25) * mm, "end": v(22.1, 92.25) * mm});
            skCircle(sketch, "E82", {"center": v(0, 104.25) * mm, "radius": 6 * mm});
            skLineSegment(sketch, "E83", {"start": v(-7.7, 92.25) * mm, "end": v(-7.7, 104.25) * mm});
            skLineSegment(sketch, "E84", {"start": v(22.1, 92.25) * mm, "end": v(22.1, 100.96) * mm});
            skArc(sketch, "E85", {"start": v(22.1, 100.96) * mm, "mid": v(8.92, 118.17) * mm, "end": v(-7.7, 104.25) * mm});
            skSolve(sketch);
        }
        {
            var Q0;
            {var subQ3=sQuery(id+"F16.wireOp",EDGE,"E80");Q0=makeQuery(id+"F16.imprint","IMPRINT",FACE,{"disambiguationData":[TD([[makeQuery(id+"F16.imprint","IMPRINT",EDGE,{"derivedFrom":subQ3}),-1.0]])]});}
            var Q1;
            Q1=makeQuery(id+"F16.imprint","IMPRINT",FACE,{"disambiguationData":[TD([[makeQuery(id+"F16.imprint","IMPRINT",EDGE,{"derivedFrom":sQuery(id+"F16.wireOp",EDGE,"E82")}),1.0]])]});
            extrude(context, id + "F17", {"entities" : qUnion([Q0, Q1]), "depth" : 25 * mm});
        }
    });
